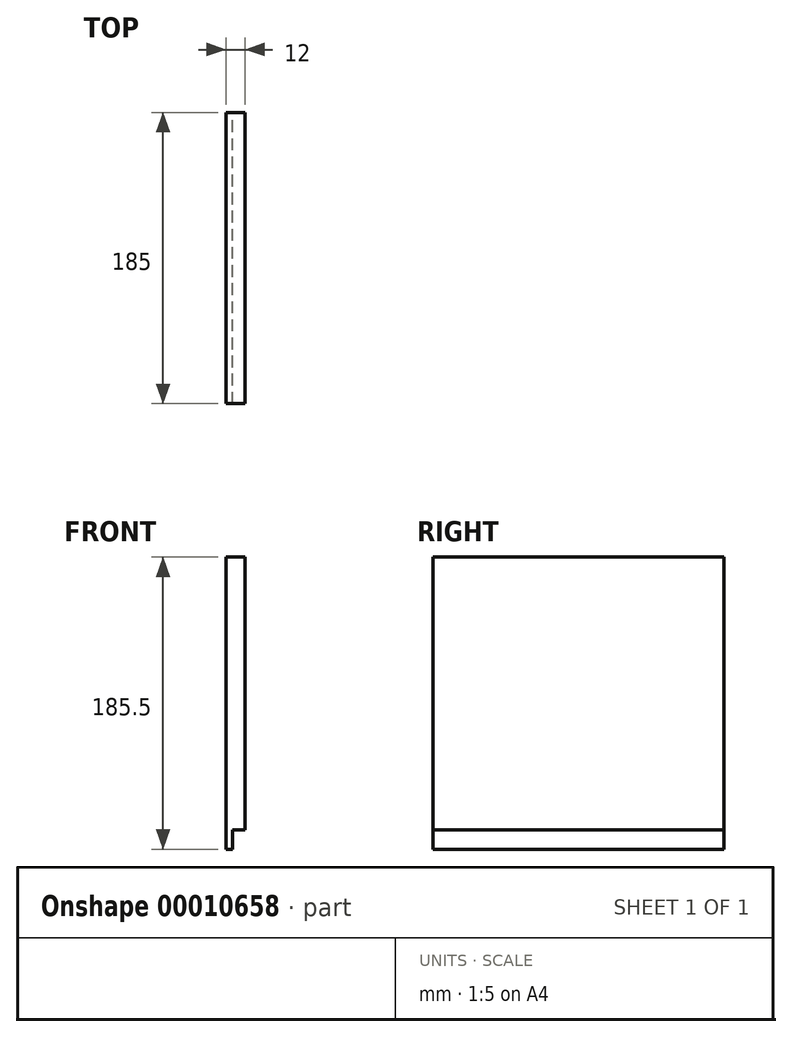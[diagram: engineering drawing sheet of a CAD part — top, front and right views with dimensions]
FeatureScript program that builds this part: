
annotation { "Feature Type Name" : "Feature", "Feature Type Description" : "" }
export const myFeature = defineFeature(function(context is Context, id is Id, definition is map)
    precondition{}
    {
        {
            var Q0;
            Q0=qCreatedBy(makeId("Right.planeOp"),FACE);
            var sketch = newSketch(context, id + "F0", { "sketchPlane" : qUnion([Q0])});
            skLineSegment(sketch, "E0.bottom", {"start": v(0, 0) * mm, "end": v(185, 0) * mm});
            skLineSegment(sketch, "E0.top", {"start": v(0, 185.5) * mm, "end": v(185, 185.5) * mm});
            skLineSegment(sketch, "E0.left", {"start": v(0, 0) * mm, "end": v(0, 185.5) * mm});
            skLineSegment(sketch, "E0.right", {"start": v(185, 0) * mm, "end": v(185, 185.5) * mm});
            skSolve(sketch);
        }
        {
            var Q0;
            Q0=makeQuery(id+"F0.imprint","IMPRINT",FACE,{"disambiguationData":[TD([[makeQuery(id+"F0.imprint","IMPRINT",EDGE,{"derivedFrom":sQuery(id+"F0.wireOp",EDGE,"E0.bottom")}),1.0]])]});
            extrude(context, id + "F1", {"entities" : qUnion([Q0]), "depth" : 12 * mm});
        }
        {
            var Q0;
            Q0=makeQuery(id+"F1.opExtrude","CAP_FACE",FACE,{"disambiguationData":[OSD([sQuery(id+"F0.wireOp",EDGE,"E0.bottom"),sQuery(id+"F0.wireOp",EDGE,"E0.top"),sQuery(id+"F0.wireOp",EDGE,"E0.left"),sQuery(id+"F0.wireOp",EDGE,"E0.right")])],"isStart":false});
            var sketch = newSketch(context, id + "F2", { "sketchPlane" : qUnion([Q0])});
            skLineSegment(sketch, "E1.bottom", {"start": v(0, 0) * mm, "end": v(185, 0) * mm});
            skLineSegment(sketch, "E1.top", {"start": v(0, 12.2) * mm, "end": v(185, 12.2) * mm});
            skLineSegment(sketch, "E1.left", {"start": v(0, 0) * mm, "end": v(0, 12.2) * mm});
            skLineSegment(sketch, "E1.right", {"start": v(185, 0) * mm, "end": v(185, 12.2) * mm});
            skSolve(sketch);
        }
        {
            var Q0;
            Q0=makeQuery(id+"F2.imprint","IMPRINT",FACE,{"disambiguationData":[TD([[makeQuery(id+"F2.imprint","IMPRINT",EDGE,{"derivedFrom":sQuery(id+"F2.wireOp",EDGE,"E1.bottom")}),1.0]])]});
            extrude(context, id + "F3", {"entities" : qUnion([Q0]), "operationType" : NewBodyOperationType.REMOVE, "oppositeDirection" : true, "depth" : 8 * mm});
        }
        {
            var Q0;
            Q0=makeQuery(id+"F1.opExtrude","SWEPT_BODY",BODY,{"disambiguationData":[OSD([sQuery(id+"F0.wireOp",EDGE,"E0.bottom"),sQuery(id+"F0.wireOp",EDGE,"E0.top"),sQuery(id+"F0.wireOp",EDGE,"E0.left"),sQuery(id+"F0.wireOp",EDGE,"E0.right")])]});
            transform(context, id + "F4", {"entities" : qUnion([Q0]), "transformType" : TransformType.TRANSLATION_3D, "dx" : 0 * mm, "dy" : 0 * mm, "dz" : 0 * mm, "makeCopy" : true});
        }
    });
